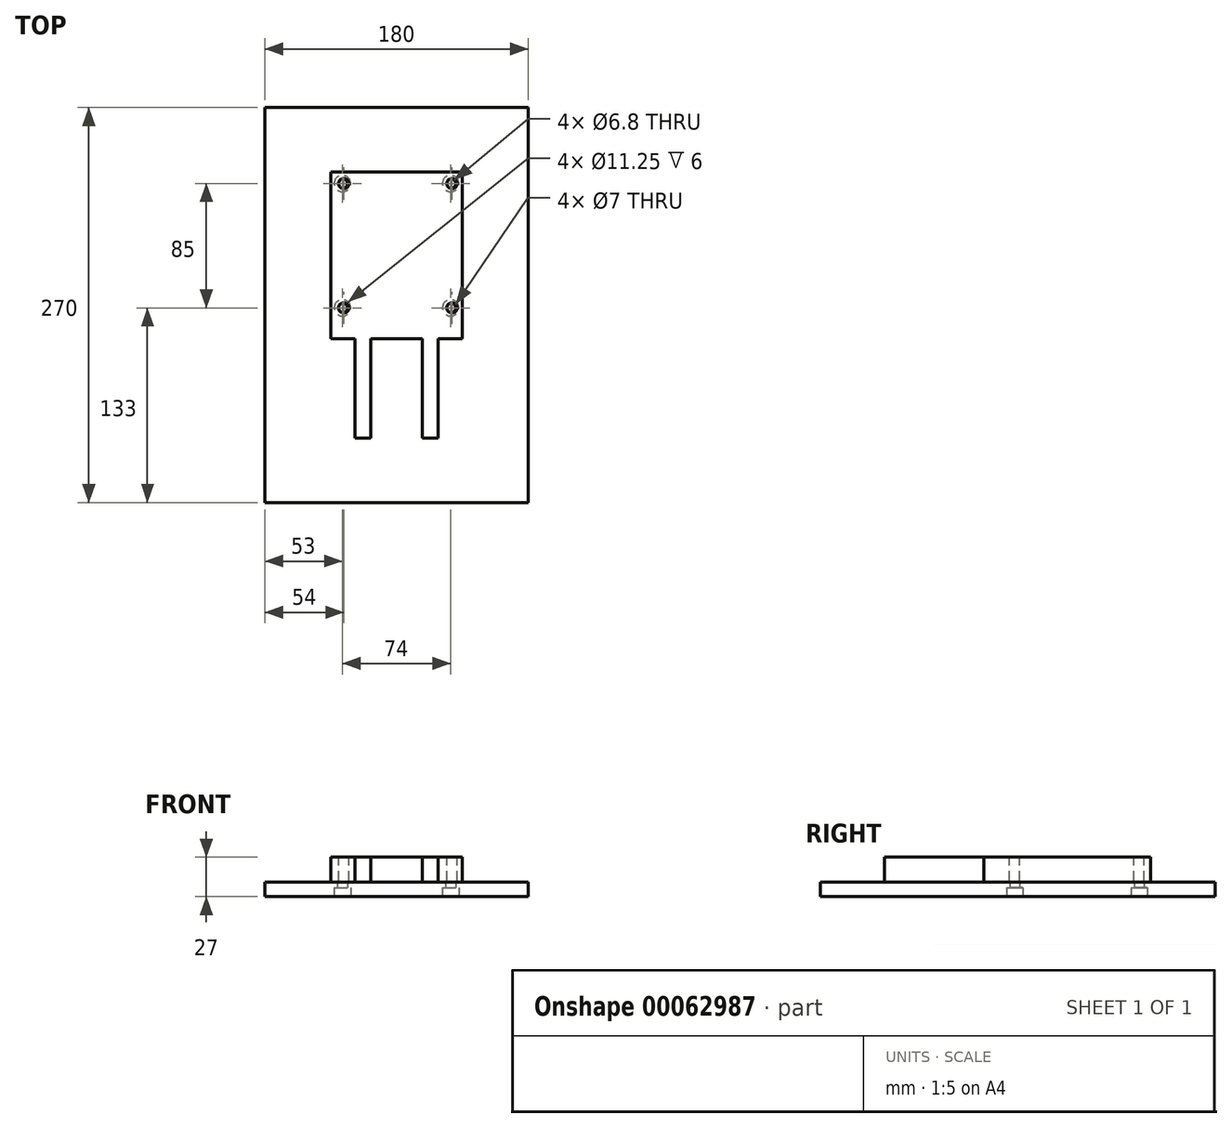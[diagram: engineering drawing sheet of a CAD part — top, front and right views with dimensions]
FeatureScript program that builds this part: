
annotation { "Feature Type Name" : "Feature", "Feature Type Description" : "" }
export const myFeature = defineFeature(function(context is Context, id is Id, definition is map)
    precondition{}
    {
        {
            var Q0;
            Q0=qCreatedBy(makeId("Top.planeOp"),FACE);
            var sketch = newSketch(context, id + "F0", { "sketchPlane" : qUnion([Q0])});
            skLineSegment(sketch, "E0.bottom", {"start": v(-45, 0) * mm, "end": v(-28.5, 0) * mm});
            skLineSegment(sketch, "E0.top", {"start": v(-45, 114) * mm, "end": v(45, 114) * mm});
            skLineSegment(sketch, "E0.left", {"start": v(-45, 0) * mm, "end": v(-45, 114) * mm});
            skLineSegment(sketch, "E0.right", {"start": v(45, 0) * mm, "end": v(45, 114) * mm});
            skLineSegment(sketch, "E1", {"start": v(-28.5, 0) * mm, "end": v(-28.5, -68) * mm});
            skLineSegment(sketch, "E2", {"start": v(-28.5, -68) * mm, "end": v(-17.5, -68) * mm});
            skLineSegment(sketch, "E3", {"start": v(-17.5, -68) * mm, "end": v(-17.5, 0) * mm});
            skLineSegment(sketch, "E4", {"start": v(17.5, 0) * mm, "end": v(17.5, -68) * mm});
            skLineSegment(sketch, "E5", {"start": v(17.5, -68) * mm, "end": v(28.5, -68) * mm});
            skLineSegment(sketch, "E6", {"start": v(28.5, -68) * mm, "end": v(28.5, 0) * mm});
            skLineSegment(sketch, "E7.trimOffspring", {"start": v(-17.5, 0) * mm, "end": v(17.5, 0) * mm});
            skLineSegment(sketch, "E8.trimOffspring", {"start": v(28.5, 0) * mm, "end": v(45, 0) * mm});
            skSolve(sketch);
        }
        {
            var Q0;
            Q0=makeQuery(id+"F0.imprint","IMPRINT",FACE,{"disambiguationData":[TD([[makeQuery(id+"F0.imprint","IMPRINT",EDGE,{"derivedFrom":sQuery(id+"F0.wireOp",EDGE,"E0.bottom")}),1.0]])]});
            extrude(context, id + "F1", {"entities" : qUnion([Q0]), "depth" : 17 * mm});
        }
        {
            var Q0;
            Q0=makeQuery(id+"F1.opExtrude","CAP_FACE",FACE,{"disambiguationData":[OSD([sQuery(id+"F0.wireOp",EDGE,"E0.bottom"),sQuery(id+"F0.wireOp",EDGE,"E0.top"),sQuery(id+"F0.wireOp",EDGE,"E0.left"),sQuery(id+"F0.wireOp",EDGE,"E0.right"),sQuery(id+"F0.wireOp",EDGE,"E1"),sQuery(id+"F0.wireOp",EDGE,"E2"),sQuery(id+"F0.wireOp",EDGE,"E3"),sQuery(id+"F0.wireOp",EDGE,"E4"),sQuery(id+"F0.wireOp",EDGE,"E5"),sQuery(id+"F0.wireOp",EDGE,"E6"),sQuery(id+"F0.wireOp",EDGE,"E7.trimOffspring"),sQuery(id+"F0.wireOp",EDGE,"E8.trimOffspring")])],"isStart":false});
            var sketch = newSketch(context, id + "F2", { "sketchPlane" : qUnion([Q0])});
            skCircle(sketch, "E9", {"center": v(-36, 106) * mm, "radius": 3.5 * mm});
            skCircle(sketch, "E10", {"center": v(-36, 21) * mm, "radius": 3.5 * mm});
            skCircle(sketch, "E11", {"center": v(38, 106) * mm, "radius": 3.5 * mm});
            skCircle(sketch, "E12", {"center": v(38, 21) * mm, "radius": 3.5 * mm});
            skSolve(sketch);
        }
        {
            var Q0;
            Q0 = qSketchRegion(id + "F2", true);
            extrude(context, id + "F3", {"entities" : qUnion([Q0]), "operationType" : NewBodyOperationType.REMOVE, "endBound" : BoundingType.THROUGH_ALL, "oppositeDirection" : true, "depth" : 25 * mm});
        }
        {
            var Q0;
            Q0=qCreatedBy(makeId("Top.planeOp"),FACE);
            var sketch = newSketch(context, id + "F4", { "sketchPlane" : qUnion([Q0])});
            skLineSegment(sketch, "E13.bottom", {"start": v(90, 158) * mm, "end": v(-90, 158) * mm});
            skLineSegment(sketch, "E13.top", {"start": v(90, -112) * mm, "end": v(-90, -112) * mm});
            skLineSegment(sketch, "E13.left", {"start": v(90, 158) * mm, "end": v(90, -112) * mm});
            skLineSegment(sketch, "E13.right", {"start": v(-90, 158) * mm, "end": v(-90, -112) * mm});
            skSolve(sketch);
        }
        {
            var Q0;
            Q0 = qSketchRegion(id + "F4", true);
            extrude(context, id + "F5", {"entities" : qUnion([Q0]), "oppositeDirection" : true, "depth" : 10 * mm});
        }
        {
            var Q0;
            Q0=makeQuery(id+"F5.opExtrude","CAP_FACE",FACE,{"disambiguationData":[OSD([sQuery(id+"F4.wireOp",EDGE,"E13.bottom"),sQuery(id+"F4.wireOp",EDGE,"E13.top"),sQuery(id+"F4.wireOp",EDGE,"E13.left"),sQuery(id+"F4.wireOp",EDGE,"E13.right")])],"isStart":false});
            var sketch = newSketch(context, id + "F6", { "sketchPlane" : qUnion([Q0])});
            skCircle(sketch, "E14", {"center": v(37, -106) * mm, "radius": 3.4 * mm});
            skCircle(sketch, "E15", {"center": v(-37, -106) * mm, "radius": 3.4 * mm});
            skCircle(sketch, "E16", {"center": v(37, -21) * mm, "radius": 3.4 * mm});
            skCircle(sketch, "E17", {"center": v(-37, -21) * mm, "radius": 3.4 * mm});
            skSolve(sketch);
        }
        {
            var Q0;
            Q0 = qSketchRegion(id + "F6", true);
            extrude(context, id + "F7", {"entities" : qUnion([Q0]), "operationType" : NewBodyOperationType.REMOVE, "oppositeDirection" : true, "depth" : 10 * mm});
        }
        {
            var Q0;
            Q0=makeQuery(id+"F5.opExtrude","CAP_FACE",FACE,{"disambiguationData":[OSD([sQuery(id+"F4.wireOp",EDGE,"E13.bottom"),sQuery(id+"F4.wireOp",EDGE,"E13.top"),sQuery(id+"F4.wireOp",EDGE,"E13.left"),sQuery(id+"F4.wireOp",EDGE,"E13.right")])],"isStart":false});
            var sketch = newSketch(context, id + "F8", { "sketchPlane" : qUnion([Q0])});
            skCircle(sketch, "E18", {"center": v(37, -21) * mm, "radius": 5.62 * mm});
            skCircle(sketch, "E19", {"center": v(37, -106) * mm, "radius": 5.62 * mm});
            skCircle(sketch, "E20", {"center": v(-37, -106) * mm, "radius": 5.62 * mm});
            skCircle(sketch, "E21", {"center": v(-37, -21) * mm, "radius": 5.62 * mm});
            skSolve(sketch);
        }
        {
            var Q0;
            Q0 = qSketchRegion(id + "F8", true);
            extrude(context, id + "F9", {"entities" : qUnion([Q0]), "operationType" : NewBodyOperationType.REMOVE, "oppositeDirection" : true, "depth" : 6 * mm});
        }
    });
